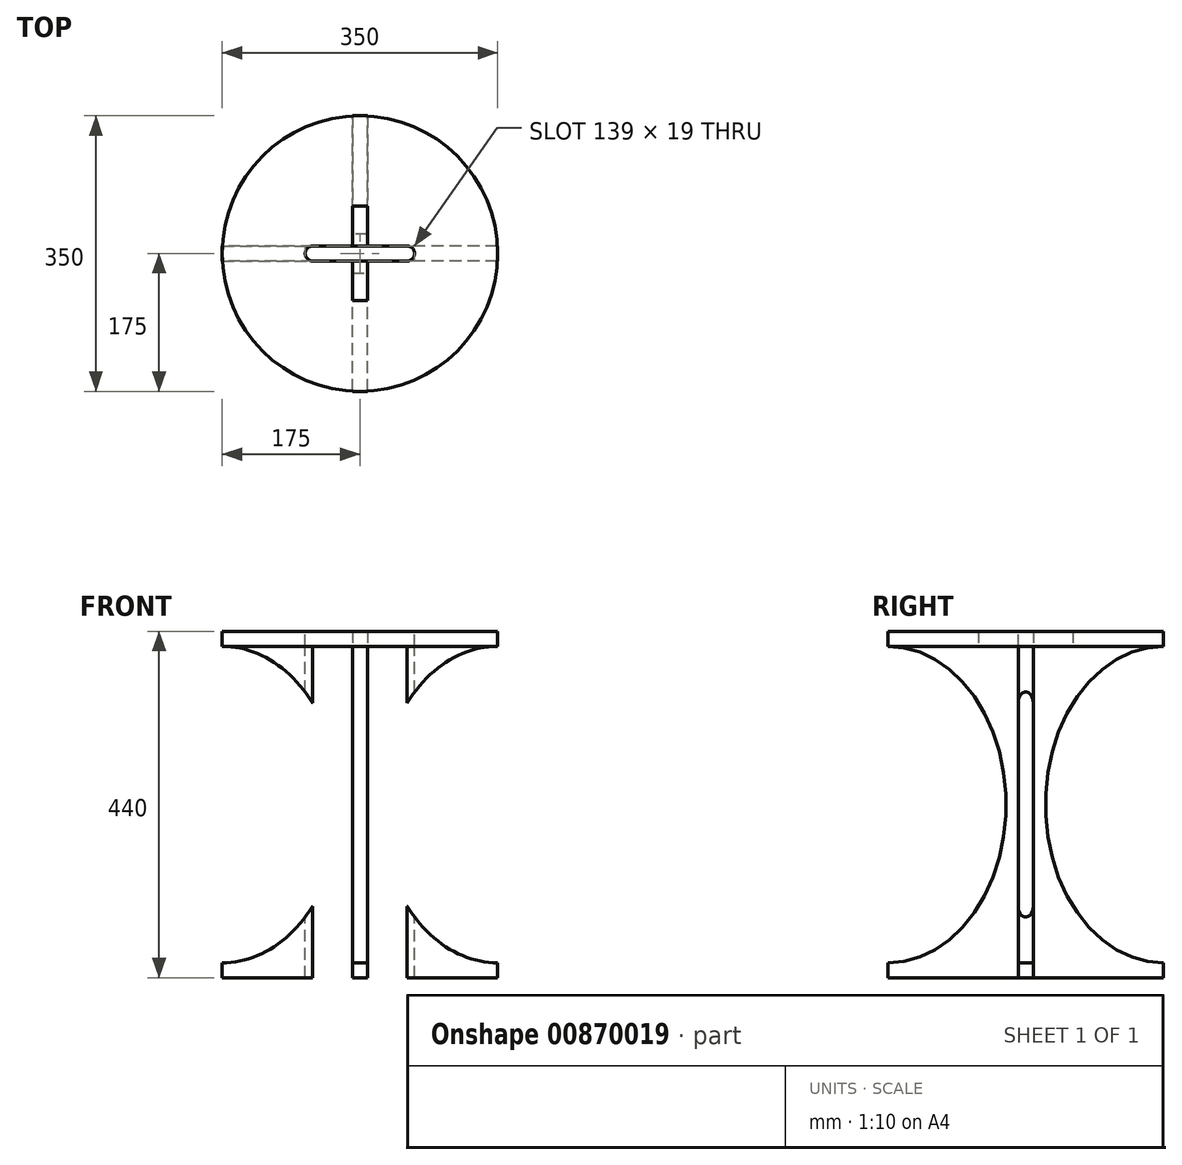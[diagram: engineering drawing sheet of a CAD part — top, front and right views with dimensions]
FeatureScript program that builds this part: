
annotation { "Feature Type Name" : "Feature", "Feature Type Description" : "" }
export const myFeature = defineFeature(function(context is Context, id is Id, definition is map)
    precondition{}
    {
        {
            var Q0;
            Q0=qCreatedBy(makeId("Front.planeOp"),FACE);
            var sketch = newSketch(context, id + "F0", { "sketchPlane" : qUnion([Q0])});
            skLineSegment(sketch, "E0.bottom", {"start": v(0, 220) * mm, "end": v(-175, 220) * mm});
            skLineSegment(sketch, "E0.top", {"start": v(0, -220) * mm, "end": v(-175, -220) * mm});
            skLineSegment(sketch, "E0.left", {"start": v(0, 220) * mm, "end": v(0, -220) * mm});
            skLineSegment(sketch, "E0.right", {"start": v(-175, 220) * mm, "end": v(-175, -220) * mm});
            skEllipse(sketch, "E1", {"center": v(-175, 0) * mm, "majorRadius": 201 * mm, "minorRadius": 150 * mm, "majorAxis": v(0, -1)});
            skLineSegment(sketch, "E2.bottom", {"start": v(-175, 220) * mm, "end": v(-60, 220) * mm});
            skLineSegment(sketch, "E2.top", {"start": v(-175, 201) * mm, "end": v(-60, 201) * mm});
            skLineSegment(sketch, "E2.left", {"start": v(-175, 220) * mm, "end": v(-175, 201) * mm});
            skLineSegment(sketch, "E2.right", {"start": v(-60, 220) * mm, "end": v(-60, 201) * mm});
            skSolve(sketch);
        }
        {
            var Q0;
            {var subQ1=sQuery(id+"F0.wireOp",EDGE,"E0.top");Q0=makeQuery(id+"F0.imprint","IMPRINT",FACE,{"disambiguationData":[TD([[makeQuery(id+"F0.imprint","IMPRINT",EDGE,{"derivedFrom":subQ1}),-1.0]])]});}
            extrude(context, id + "F1", {"entities" : qUnion([Q0]), "depth" : (19 / 2) * mm, "offsetDistance" : 25 * mm, "hasSecondDirection" : true, "secondDirectionOppositeDirection" : true, "secondDirectionDepth" : (19 / 2) * mm});
        }
        {
            var Q0;
            Q0=makeQuery(id+"F1.opExtrude","SWEPT_BODY",BODY,{"disambiguationData":[OSD([sQuery(id+"F0.wireOp",EDGE,"E0.bottom"),sQuery(id+"F0.wireOp",EDGE,"E0.top"),sQuery(id+"F0.wireOp",EDGE,"E0.left"),sQuery(id+"F0.wireOp",EDGE,"E0.right"),sQuery(id+"F0.wireOp",EDGE,"E1"),sQuery(id+"F0.wireOp",EDGE,"E2.top"),sQuery(id+"F0.wireOp",EDGE,"E2.right")])]});
            var Q1;
            Q1=qCreatedBy(makeId("Right.planeOp"),FACE);
            mirror(context, id + "F2", {"operationType" : NewBodyOperationType.ADD, "entities" : qUnion([Q0]), "mirrorPlane" : qUnion([Q1])});
        }
        {
            var Q0;
            Q0=qCreatedBy(makeId("Right.planeOp"),FACE);
            var Q1;
            Q1=qCreatedBy(makeId("Front.planeOp"),FACE);
            cPlane(context, id + "F3", {"entities" : qUnion([Q0, Q1]), "cplaneType" : CPlaneType.MID_PLANE, "offset" : 25 * mm, "width" : 150 * mm, "height" : 150 * mm});
        }
        {
            var Q0;
            Q0=makeQuery(id+"F1.opExtrude","SWEPT_BODY",BODY,{"disambiguationData":[OSD([sQuery(id+"F0.wireOp",EDGE,"E0.bottom"),sQuery(id+"F0.wireOp",EDGE,"E0.top"),sQuery(id+"F0.wireOp",EDGE,"E0.left"),sQuery(id+"F0.wireOp",EDGE,"E0.right"),sQuery(id+"F0.wireOp",EDGE,"E1"),sQuery(id+"F0.wireOp",EDGE,"E2.top"),sQuery(id+"F0.wireOp",EDGE,"E2.right")])]});
            var Q1;
            Q1=qCreatedBy(id+"F3.planeOp",FACE);
            mirror(context, id + "F4", {"entities" : qUnion([Q0]), "mirrorPlane" : qUnion([Q1])});
        }
        {
            var Q0;
            {var subQ0=makeQuery(id+"F1.opExtrude","SWEPT_FACE",FACE,{"disambiguationData":[OSD([sQuery(id+"F0.wireOp",EDGE,"E0.bottom")])]});Q0=makeQuery(id+"F2.boolean.opBoolean","MERGE",FACE,{"derivedFrom":[subQ0,makeQuery(id+"F2.opPattern","COPY",FACE,{"derivedFrom":subQ0,"instanceName":"1"})]});}
            var sketch = newSketch(context, id + "F5", { "sketchPlane" : qUnion([Q0])});
            skCircle(sketch, "E3", {"center": v(0, 0) * mm, "radius": 175 * mm});
            skSolve(sketch);
        }
        {
            var Q0;
            Q0 = qSketchRegion(id + "F5", true);
            extrude(context, id + "F6", {"entities" : qUnion([Q0]), "oppositeDirection" : true, "depth" : 19 * mm, "offsetDistance" : 25 * mm});
        }
        {
            var Q0;
            Q0=makeQuery(id+"F6.opExtrude","CAP_FACE",FACE,{"disambiguationData":[OSD([sQuery(id+"F5.wireOp",EDGE,"E3")])],"isStart":true});
            var sketch = newSketch(context, id + "F7", { "sketchPlane" : qUnion([Q0])});
            skLineSegment(sketch, "E4.bottom", {"start": v(-60, -9.5) * mm, "end": v(60, -9.5) * mm});
            skLineSegment(sketch, "E4.top", {"start": v(-60, 9.5) * mm, "end": v(60, 9.5) * mm});
            skLineSegment(sketch, "E4.left", {"start": v(-60, -9.5) * mm, "end": v(-60, 9.5) * mm});
            skLineSegment(sketch, "E4.right", {"start": v(60, -9.5) * mm, "end": v(60, 9.5) * mm});
            skPoint(sketch, "E4.middle", {"position": v(0, 0) * mm});
            skArc(sketch, "E5", {"start": v(-60, 9.5) * mm, "mid": v(-69.5, 0) * mm, "end": v(-60, -9.5) * mm});
            skArc(sketch, "E6", {"start": v(60, -9.5) * mm, "mid": v(69.5, 0) * mm, "end": v(60, 9.5) * mm});
            skSolve(sketch);
        }
        {
            var Q0;
            Q0 = qSketchRegion(id + "F7", true);
            extrude(context, id + "F8", {"entities" : qUnion([Q0]), "operationType" : NewBodyOperationType.REMOVE, "endBound" : BoundingType.THROUGH_ALL, "oppositeDirection" : true, "depth" : 25 * mm, "offsetDistance" : 25 * mm});
        }
    });
